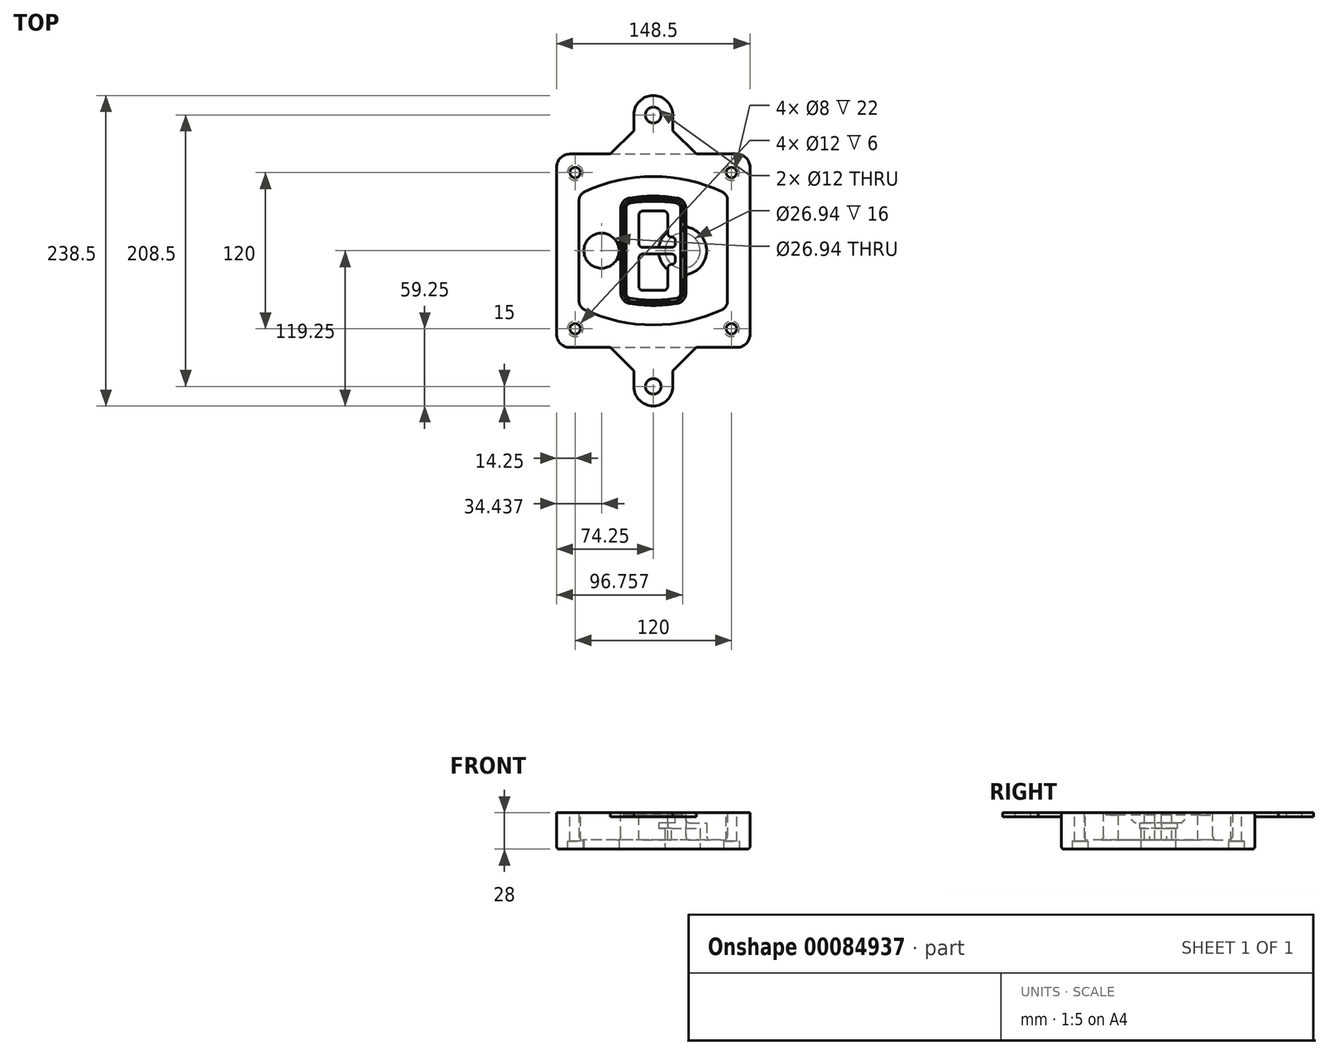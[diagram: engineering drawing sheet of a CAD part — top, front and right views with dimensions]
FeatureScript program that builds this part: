
annotation { "Feature Type Name" : "Feature", "Feature Type Description" : "" }
export const myFeature = defineFeature(function(context is Context, id is Id, definition is map)
    precondition{}
    {
        {
            var Q0;
            Q0=qCreatedBy(makeId("Top.planeOp"),FACE);
            var sketch = newSketch(context, id + "F0", { "sketchPlane" : qUnion([Q0])});
            skPoint(sketch, "E0.rect.middle", {"position": v(0, 0) * mm});
            skLineSegment(sketch, "E1.bottom", {"start": v(-64.25, -74.25) * mm, "end": v(64.25, -74.25) * mm});
            skLineSegment(sketch, "E1.top", {"start": v(-64.25, 74.25) * mm, "end": v(64.25, 74.25) * mm});
            skLineSegment(sketch, "E1.left", {"start": v(-74.25, -64.25) * mm, "end": v(-74.25, 64.25) * mm});
            skLineSegment(sketch, "E1.right", {"start": v(74.25, -64.25) * mm, "end": v(74.25, 64.25) * mm});
            skLineSegment(sketch, "E2", {"start": v(-74.25, 74.25) * mm, "end": v(74.25, -74.25) * mm, "construction": true});
            skLineSegment(sketch, "E3", {"start": v(74.25, 74.25) * mm, "end": v(-74.25, -74.25) * mm, "construction": true});
            skCircle(sketch, "E4", {"center": v(-60, 60) * mm, "radius": 4 * mm});
            skCircle(sketch, "E5", {"center": v(60, 60) * mm, "radius": 4 * mm});
            skCircle(sketch, "E6", {"center": v(60, -60) * mm, "radius": 4 * mm});
            skCircle(sketch, "E7", {"center": v(-60, -60) * mm, "radius": 4 * mm});
            skLineSegment(sketch, "E8", {"start": v(-60, 60) * mm, "end": v(60, 60) * mm, "construction": true});
            skLineSegment(sketch, "E9", {"start": v(60, 60) * mm, "end": v(60, -60) * mm, "construction": true});
            skLineSegment(sketch, "E10", {"start": v(60, -60) * mm, "end": v(-60, -60) * mm, "construction": true});
            skLineSegment(sketch, "E11", {"start": v(-60, -60) * mm, "end": v(-60, 60) * mm, "construction": true});
            skLineSegment(sketch, "E12", {"start": v(-60, 38.83) * mm, "end": v(-60, -38.83) * mm});
            skLineSegment(sketch, "E13", {"start": v(60, 38.83) * mm, "end": v(60, -38.83) * mm});
            skArc(sketch, "E14", {"start": v(54.26, 47.88) * mm, "mid": v(0, 60) * mm, "end": v(-54.26, 47.88) * mm});
            skArc(sketch, "E15", {"start": v(-54.26, -47.88) * mm, "mid": v(0, -60) * mm, "end": v(54.26, -47.88) * mm});
            skLineSegment(sketch, "E16", {"start": v(-60, 0) * mm, "end": v(60, 0) * mm, "construction": true});
            skPoint(sketch, "E17.visualSharp", {"position": v(-60, -45) * mm});
            skArc(sketch, "E17.filletArc", {"start": v(-60, -38.83) * mm, "mid": v(-58.44, -44.2) * mm, "end": v(-54.26, -47.88) * mm});
            skPoint(sketch, "E18.visualSharp", {"position": v(-60, 45) * mm});
            skArc(sketch, "E18.filletArc", {"start": v(-54.26, 47.88) * mm, "mid": v(-58.44, 44.2) * mm, "end": v(-60, 38.83) * mm});
            skPoint(sketch, "E19.visualSharp", {"position": v(60, 45) * mm});
            skArc(sketch, "E19.filletArc", {"start": v(60, 38.83) * mm, "mid": v(58.44, 44.2) * mm, "end": v(54.26, 47.88) * mm});
            skPoint(sketch, "E20.visualSharp", {"position": v(60, -45) * mm});
            skArc(sketch, "E20.filletArc", {"start": v(54.26, -47.88) * mm, "mid": v(58.44, -44.2) * mm, "end": v(60, -38.83) * mm});
            skPoint(sketch, "E21.visualSharp", {"position": v(-74.25, 74.25) * mm});
            skArc(sketch, "E21.filletArc", {"start": v(-64.25, 74.25) * mm, "mid": v(-71.32, 71.32) * mm, "end": v(-74.25, 64.25) * mm});
            skPoint(sketch, "E22.visualSharp", {"position": v(74.25, 74.25) * mm});
            skArc(sketch, "E22.filletArc", {"start": v(74.25, 64.25) * mm, "mid": v(71.32, 71.32) * mm, "end": v(64.25, 74.25) * mm});
            skPoint(sketch, "E23.visualSharp", {"position": v(74.25, -74.25) * mm});
            skArc(sketch, "E23.filletArc", {"start": v(64.25, -74.25) * mm, "mid": v(71.32, -71.32) * mm, "end": v(74.25, -64.25) * mm});
            skPoint(sketch, "E24.visualSharp", {"position": v(-74.25, -74.25) * mm});
            skArc(sketch, "E24.filletArc", {"start": v(-74.25, -64.25) * mm, "mid": v(-71.32, -71.32) * mm, "end": v(-64.25, -74.25) * mm});
            skArc(sketch, "E25.0", {"start": v(57, 38.83) * mm, "mid": v(55.9, 42.58) * mm, "end": v(52.98, 45.17) * mm});
            skLineSegment(sketch, "E25.1", {"start": v(57, 38.83) * mm, "end": v(57, -38.83) * mm});
            skArc(sketch, "E25.2", {"start": v(52.98, -45.17) * mm, "mid": v(55.9, -42.58) * mm, "end": v(57, -38.83) * mm});
            skArc(sketch, "E25.3", {"start": v(-52.98, -45.17) * mm, "mid": v(0, -57) * mm, "end": v(52.98, -45.17) * mm});
            skArc(sketch, "E25.4", {"start": v(-57, -38.83) * mm, "mid": v(-55.9, -42.58) * mm, "end": v(-52.98, -45.17) * mm});
            skArc(sketch, "E25.5", {"start": v(52.98, 45.17) * mm, "mid": v(0, 57) * mm, "end": v(-52.98, 45.17) * mm});
            skLineSegment(sketch, "E25.6", {"start": v(-57, 38.83) * mm, "end": v(-57, -38.83) * mm});
            skArc(sketch, "E25.7", {"start": v(-52.98, 45.17) * mm, "mid": v(-55.9, 42.58) * mm, "end": v(-57, 38.83) * mm});
            skArc(sketch, "E26.0", {"start": v(-55.96, 51.5) * mm, "mid": v(-61.82, 46.33) * mm, "end": v(-64, 38.83) * mm});
            skArc(sketch, "E26.1", {"start": v(55.96, 51.5) * mm, "mid": v(0, 64) * mm, "end": v(-55.96, 51.5) * mm});
            skArc(sketch, "E26.2", {"start": v(64, 38.83) * mm, "mid": v(61.82, 46.33) * mm, "end": v(55.96, 51.5) * mm});
            skLineSegment(sketch, "E26.3", {"start": v(64, 38.83) * mm, "end": v(64, -38.83) * mm});
            skArc(sketch, "E26.4", {"start": v(55.96, -51.5) * mm, "mid": v(61.82, -46.33) * mm, "end": v(64, -38.83) * mm});
            skLineSegment(sketch, "E26.5", {"start": v(-64, 38.83) * mm, "end": v(-64, -38.83) * mm});
            skArc(sketch, "E26.6", {"start": v(-55.96, -51.5) * mm, "mid": v(0, -64) * mm, "end": v(55.96, -51.5) * mm});
            skArc(sketch, "E26.7", {"start": v(-64, -38.83) * mm, "mid": v(-61.82, -46.33) * mm, "end": v(-55.96, -51.5) * mm});
            skSolve(sketch);
        }
        {
            var Q0;
            Q0=makeQuery(id+"F0.imprint","IMPRINT",FACE,{"disambiguationData":[TD([[makeQuery(id+"F0.imprint","IMPRINT",EDGE,{"derivedFrom":sQuery(id+"F0.wireOp",EDGE,"E1.bottom")}),1.0]])]});
            var Q1;
            Q1=makeQuery(id+"F0.imprint","IMPRINT",FACE,{"disambiguationData":[TD([[makeQuery(id+"F0.imprint","IMPRINT",EDGE,{"derivedFrom":sQuery(id+"F0.wireOp",EDGE,"E12")}),1.0]])]});
            var Q2;
            Q2=makeQuery(id+"F0.imprint","IMPRINT",FACE,{"disambiguationData":[TD([[makeQuery(id+"F0.imprint","IMPRINT",EDGE,{"derivedFrom":sQuery(id+"F0.wireOp",EDGE,"E25.0")}),1.0]])]});
            var Q3;
            Q3=makeQuery(id+"F0.imprint","IMPRINT",FACE,{"disambiguationData":[TD([[makeQuery(id+"F0.imprint","IMPRINT",EDGE,{"derivedFrom":sQuery(id+"F0.wireOp",EDGE,"E12")}),-1.0]])]});
            extrude(context, id + "F1", {"entities" : qUnion([Q0, Q1, Q2, Q3]), "oppositeDirection" : true, "depth" : 25 * mm});
        }
        {
            var Q0;
            Q0=makeQuery(id+"F0.imprint","IMPRINT",FACE,{"disambiguationData":[TD([[makeQuery(id+"F0.imprint","IMPRINT",EDGE,{"derivedFrom":sQuery(id+"F0.wireOp",EDGE,"E12")}),1.0]])]});
            extrude(context, id + "F2", {"entities" : qUnion([Q0]), "operationType" : NewBodyOperationType.ADD, "depth" : 3 * mm});
        }
        {
            var Q0;
            Q0=makeQuery(id+"F0.imprint","IMPRINT",FACE,{"disambiguationData":[TD([[makeQuery(id+"F0.imprint","IMPRINT",EDGE,{"derivedFrom":sQuery(id+"F0.wireOp",EDGE,"E25.0")}),1.0]])]});
            extrude(context, id + "F3", {"entities" : qUnion([Q0]), "operationType" : NewBodyOperationType.REMOVE, "oppositeDirection" : true, "depth" : 18 * mm});
        }
        {
            var Q0;
            Q0=makeQuery(id+"F2.opExtrude","CAP_FACE",FACE,{"disambiguationData":[OSD([sQuery(id+"F0.wireOp",EDGE,"E12"),sQuery(id+"F0.wireOp",EDGE,"E13"),sQuery(id+"F0.wireOp",EDGE,"E14"),sQuery(id+"F0.wireOp",EDGE,"E15"),sQuery(id+"F0.wireOp",EDGE,"E17.filletArc"),sQuery(id+"F0.wireOp",EDGE,"E18.filletArc"),sQuery(id+"F0.wireOp",EDGE,"E19.filletArc"),sQuery(id+"F0.wireOp",EDGE,"E20.filletArc"),sQuery(id+"F0.wireOp",EDGE,"E25.0"),sQuery(id+"F0.wireOp",EDGE,"E25.1"),sQuery(id+"F0.wireOp",EDGE,"E25.2"),sQuery(id+"F0.wireOp",EDGE,"E25.3"),sQuery(id+"F0.wireOp",EDGE,"E25.4"),sQuery(id+"F0.wireOp",EDGE,"E25.5"),sQuery(id+"F0.wireOp",EDGE,"E25.6"),sQuery(id+"F0.wireOp",EDGE,"E25.7")])],"isStart":false});
            var sketch = newSketch(context, id + "F4", { "sketchPlane" : qUnion([Q0])});
            skArc(sketch, "E27.0", {"start": v(-18.34, -40.45) * mm, "mid": v(0, -42) * mm, "end": v(18.34, -40.45) * mm});
            skArc(sketch, "E28.0", {"start": v(18.34, 40.45) * mm, "mid": v(0, 42) * mm, "end": v(-18.34, 40.45) * mm});
            skLineSegment(sketch, "E29", {"start": v(-25, 32.57) * mm, "end": v(-25, -32.57) * mm});
            skLineSegment(sketch, "E30", {"start": v(25, 32.57) * mm, "end": v(25, -32.57) * mm});
            skLineSegment(sketch, "E31", {"start": v(-25, 39.1) * mm, "end": v(25, 39.1) * mm, "construction": true});
            skLineSegment(sketch, "E32", {"start": v(-25, -39.1) * mm, "end": v(25, -39.1) * mm, "construction": true});
            skPoint(sketch, "E33.visualSharp", {"position": v(-25, 39.1) * mm});
            skArc(sketch, "E33.filletArc", {"start": v(-18.34, 40.45) * mm, "mid": v(-23.11, 37.73) * mm, "end": v(-25, 32.57) * mm});
            skPoint(sketch, "E34.visualSharp", {"position": v(25, 39.1) * mm});
            skArc(sketch, "E34.filletArc", {"start": v(25, 32.57) * mm, "mid": v(23.11, 37.73) * mm, "end": v(18.34, 40.45) * mm});
            skPoint(sketch, "E35.visualSharp", {"position": v(25, -39.1) * mm});
            skArc(sketch, "E35.filletArc", {"start": v(18.34, -40.45) * mm, "mid": v(23.11, -37.73) * mm, "end": v(25, -32.57) * mm});
            skPoint(sketch, "E36.visualSharp", {"position": v(-25, -39.1) * mm});
            skArc(sketch, "E36.filletArc", {"start": v(-25, -32.57) * mm, "mid": v(-23.11, -37.73) * mm, "end": v(-18.34, -40.45) * mm});
            skArc(sketch, "E37.0", {"start": v(52.98, 45.17) * mm, "mid": v(0, 57) * mm, "end": v(-52.98, 45.17) * mm});
            skArc(sketch, "E37.1", {"start": v(-52.98, 45.17) * mm, "mid": v(-55.9, 42.58) * mm, "end": v(-57, 38.83) * mm});
            skLineSegment(sketch, "E37.2", {"start": v(-57, 38.83) * mm, "end": v(-57, -38.83) * mm});
            skArc(sketch, "E37.3", {"start": v(-57, -38.83) * mm, "mid": v(-55.9, -42.58) * mm, "end": v(-52.98, -45.17) * mm});
            skArc(sketch, "E37.4", {"start": v(-52.98, -45.17) * mm, "mid": v(0, -57) * mm, "end": v(52.98, -45.17) * mm});
            skArc(sketch, "E37.5", {"start": v(52.98, -45.17) * mm, "mid": v(55.9, -42.58) * mm, "end": v(57, -38.83) * mm});
            skLineSegment(sketch, "E37.6", {"start": v(57, 38.83) * mm, "end": v(57, -38.83) * mm});
            skArc(sketch, "E37.7", {"start": v(57, 38.83) * mm, "mid": v(55.9, 42.58) * mm, "end": v(52.98, 45.17) * mm});
            skLineSegment(sketch, "E38.0", {"start": v(23, 32.57) * mm, "end": v(23, -32.57) * mm});
            skArc(sketch, "E38.1", {"start": v(18, -38.48) * mm, "mid": v(21.58, -36.44) * mm, "end": v(23, -32.57) * mm});
            skArc(sketch, "E38.2", {"start": v(-18, -38.48) * mm, "mid": v(0, -40) * mm, "end": v(18, -38.48) * mm});
            skArc(sketch, "E38.3", {"start": v(-23, -32.57) * mm, "mid": v(-21.58, -36.44) * mm, "end": v(-18, -38.48) * mm});
            skLineSegment(sketch, "E38.4", {"start": v(-23, 32.57) * mm, "end": v(-23, -32.57) * mm});
            skArc(sketch, "E38.5", {"start": v(23, 32.57) * mm, "mid": v(21.58, 36.44) * mm, "end": v(18, 38.48) * mm});
            skArc(sketch, "E38.6", {"start": v(-18, 38.48) * mm, "mid": v(-21.58, 36.44) * mm, "end": v(-23, 32.57) * mm});
            skArc(sketch, "E38.7", {"start": v(18, 38.48) * mm, "mid": v(0, 40) * mm, "end": v(-18, 38.48) * mm});
            skArc(sketch, "E39.0", {"start": v(21, 32.57) * mm, "mid": v(20.06, 35.15) * mm, "end": v(17.67, 36.5) * mm});
            skLineSegment(sketch, "E39.1", {"start": v(21, 32.57) * mm, "end": v(21, -32.57) * mm});
            skArc(sketch, "E39.2", {"start": v(17.67, -36.5) * mm, "mid": v(20.06, -35.15) * mm, "end": v(21, -32.57) * mm});
            skArc(sketch, "E39.3", {"start": v(-17.67, -36.5) * mm, "mid": v(0, -38) * mm, "end": v(17.67, -36.5) * mm});
            skArc(sketch, "E39.4", {"start": v(-21, -32.57) * mm, "mid": v(-20.06, -35.15) * mm, "end": v(-17.67, -36.5) * mm});
            skArc(sketch, "E39.5", {"start": v(17.67, 36.5) * mm, "mid": v(0, 38) * mm, "end": v(-17.67, 36.5) * mm});
            skLineSegment(sketch, "E39.6", {"start": v(-21, 32.57) * mm, "end": v(-21, -32.57) * mm});
            skArc(sketch, "E39.7", {"start": v(-17.67, 36.5) * mm, "mid": v(-20.06, 35.15) * mm, "end": v(-21, 32.57) * mm});
            skLineSegment(sketch, "E40", {"start": v(-25, 0) * mm, "end": v(25, 0) * mm, "construction": true});
            skLineSegment(sketch, "E41", {"start": v(-11, 5.5) * mm, "end": v(-11, 27.5) * mm});
            skLineSegment(sketch, "E42", {"start": v(-8, 30.5) * mm, "end": v(8, 30.5) * mm});
            skLineSegment(sketch, "E43", {"start": v(11, 27.5) * mm, "end": v(11, 13.5) * mm});
            skLineSegment(sketch, "E44", {"start": v(14, 10.5) * mm, "end": v(14, 10.5) * mm});
            skLineSegment(sketch, "E45", {"start": v(17, 7.5) * mm, "end": v(17, 5.5) * mm});
            skLineSegment(sketch, "E46", {"start": v(14, 2.5) * mm, "end": v(-8, 2.5) * mm});
            skPoint(sketch, "E47.visualSharp", {"position": v(-11, 30.5) * mm});
            skArc(sketch, "E47.filletArc", {"start": v(-8, 30.5) * mm, "mid": v(-10.12, 29.62) * mm, "end": v(-11, 27.5) * mm});
            skPoint(sketch, "E48.visualSharp", {"position": v(11, 30.5) * mm});
            skArc(sketch, "E48.filletArc", {"start": v(11, 27.5) * mm, "mid": v(10.12, 29.62) * mm, "end": v(8, 30.5) * mm});
            skPoint(sketch, "E49.visualSharp", {"position": v(11, 10.5) * mm});
            skArc(sketch, "E49.filletArc", {"start": v(11, 13.5) * mm, "mid": v(11.88, 11.38) * mm, "end": v(14, 10.5) * mm});
            skPoint(sketch, "E50.visualSharp", {"position": v(17, 10.5) * mm});
            skArc(sketch, "E50.filletArc", {"start": v(17, 7.5) * mm, "mid": v(16.12, 9.62) * mm, "end": v(14, 10.5) * mm});
            skPoint(sketch, "E51.visualSharp", {"position": v(17, 2.5) * mm});
            skArc(sketch, "E51.filletArc", {"start": v(14, 2.5) * mm, "mid": v(16.12, 3.38) * mm, "end": v(17, 5.5) * mm});
            skPoint(sketch, "E52.visualSharp", {"position": v(-11, 2.5) * mm});
            skArc(sketch, "E52.filletArc", {"start": v(-11, 5.5) * mm, "mid": v(-10.12, 3.38) * mm, "end": v(-8, 2.5) * mm});
            skLineSegment(sketch, "E53.0.MirrorCS", {"start": v(14, -2.5) * mm, "end": v(-8, -2.5) * mm});
            skArc(sketch, "E54.0.MirrorCS", {"start": v(-11, -5.5) * mm, "mid": v(-10.12, -3.38) * mm, "end": v(-8, -2.5) * mm});
            skLineSegment(sketch, "E55.0.MirrorCS", {"start": v(-11, -5.5) * mm, "end": v(-11, -27.5) * mm});
            skArc(sketch, "E56.0.MirrorCS", {"start": v(-8, -30.5) * mm, "mid": v(-10.12, -29.62) * mm, "end": v(-11, -27.5) * mm});
            skLineSegment(sketch, "E57.0.MirrorCS", {"start": v(-8, -30.5) * mm, "end": v(8, -30.5) * mm});
            skArc(sketch, "E58.0.MirrorCS", {"start": v(11, -27.5) * mm, "mid": v(10.12, -29.62) * mm, "end": v(8, -30.5) * mm});
            skLineSegment(sketch, "E59.0.MirrorCS", {"start": v(11, -27.5) * mm, "end": v(11, -13.5) * mm});
            skArc(sketch, "E60.0.MirrorCS", {"start": v(11, -13.5) * mm, "mid": v(11.88, -11.38) * mm, "end": v(14, -10.5) * mm});
            skArc(sketch, "E61.0.MirrorCS", {"start": v(17, -7.5) * mm, "mid": v(16.12, -9.62) * mm, "end": v(14, -10.5) * mm});
            skLineSegment(sketch, "E62.0.MirrorCS", {"start": v(17, -7.5) * mm, "end": v(17, -5.5) * mm});
            skArc(sketch, "E63.0.MirrorCS", {"start": v(14, -2.5) * mm, "mid": v(16.12, -3.38) * mm, "end": v(17, -5.5) * mm});
            skSolve(sketch);
        }
        {
            var Q0;
            Q0=makeQuery(id+"F4.imprint","IMPRINT",FACE,{"disambiguationData":[TD([[makeQuery(id+"F4.imprint","IMPRINT",EDGE,{"derivedFrom":sQuery(id+"F4.wireOp",EDGE,"E27.0")}),1.0]])]});
            var Q1;
            Q1=makeQuery(id+"F4.imprint","IMPRINT",FACE,{"disambiguationData":[TD([[makeQuery(id+"F4.imprint","IMPRINT",EDGE,{"derivedFrom":sQuery(id+"F4.wireOp",EDGE,"E38.0")}),-1.0]])]});
            var Q2;
            Q2=makeQuery(id+"F4.imprint","IMPRINT",FACE,{"disambiguationData":[TD([[makeQuery(id+"F4.imprint","IMPRINT",EDGE,{"derivedFrom":sQuery(id+"F4.wireOp",EDGE,"E39.0")}),1.0]])]});
            extrude(context, id + "F5", {"entities" : qUnion([Q0, Q1, Q2]), "operationType" : NewBodyOperationType.ADD, "endBound" : BoundingType.UP_TO_NEXT, "oppositeDirection" : true, "depth" : 25 * mm});
        }
        {
            var Q0;
            Q0=makeQuery(id+"F4.imprint","IMPRINT",FACE,{"disambiguationData":[TD([[makeQuery(id+"F4.imprint","IMPRINT",EDGE,{"derivedFrom":sQuery(id+"F4.wireOp",EDGE,"E38.0")}),-1.0]])]});
            extrude(context, id + "F6", {"entities" : qUnion([Q0]), "operationType" : NewBodyOperationType.REMOVE, "oppositeDirection" : true, "depth" : 2 * mm});
        }
        {
            var Q0;
            Q0=makeQuery(id+"F1.opExtrude","CAP_FACE",FACE,{"disambiguationData":[OSD([sQuery(id+"F0.wireOp",EDGE,"E1.bottom"),sQuery(id+"F0.wireOp",EDGE,"E1.top"),sQuery(id+"F0.wireOp",EDGE,"E1.left"),sQuery(id+"F0.wireOp",EDGE,"E1.right"),sQuery(id+"F0.wireOp",EDGE,"E4"),sQuery(id+"F0.wireOp",EDGE,"E5"),sQuery(id+"F0.wireOp",EDGE,"E6"),sQuery(id+"F0.wireOp",EDGE,"E7"),sQuery(id+"F0.wireOp",EDGE,"E21.filletArc"),sQuery(id+"F0.wireOp",EDGE,"E22.filletArc"),sQuery(id+"F0.wireOp",EDGE,"E23.filletArc"),sQuery(id+"F0.wireOp",EDGE,"E24.filletArc")])],"isStart":false});
            var sketch = newSketch(context, id + "F7", { "sketchPlane" : qUnion([Q0])});
            skCircle(sketch, "E64", {"center": v(22.5, 0) * mm, "radius": 13.47 * mm});
            skCircle(sketch, "E65", {"center": v(-39.81, 0) * mm, "radius": 13.47 * mm});
            skLineSegment(sketch, "E66", {"start": v(74.25, 0) * mm, "end": v(-74.25, 0) * mm});
            skCircle(sketch, "E67", {"center": v(22.5, 0) * mm, "radius": 18.47 * mm});
            skCircle(sketch, "E68", {"center": v(60, -60) * mm, "radius": 6 * mm});
            skCircle(sketch, "E69", {"center": v(-60, -60) * mm, "radius": 6 * mm});
            skCircle(sketch, "E70", {"center": v(-60, 60) * mm, "radius": 6 * mm});
            skCircle(sketch, "E71", {"center": v(60, 60) * mm, "radius": 6 * mm});
            skSolve(sketch);
        }
        {
            var Q0;
            {var subQ1=sQuery(id+"F7.wireOp",EDGE,"E66");var subQ4=sQuery(id+"F7.wireOp",EDGE,"E64");var subQ6=makeQuery(id+"F7.imprint","INTERSECT",VERTEX,{"disambiguationData":[OD(0.0)],"derivedFrom":[subQ4,subQ1]});Q0=makeQuery(id+"F7.imprint","IMPRINT",FACE,{"disambiguationData":[TD([[makeQuery(id+"F7.imprint","IMPRINT",EDGE,{"disambiguationData":[TD([[subQ6,-1.0]])],"derivedFrom":subQ4}),-1.0]])]});}
            var Q1;
            {var subQ0=sQuery(id+"F7.wireOp",EDGE,"E66");var subQ1=sQuery(id+"F7.wireOp",EDGE,"E64");var subQ3=makeQuery(id+"F7.imprint","INTERSECT",VERTEX,{"disambiguationData":[OD(0.0)],"derivedFrom":[subQ1,subQ0]});Q1=makeQuery(id+"F7.imprint","IMPRINT",FACE,{"disambiguationData":[TD([[makeQuery(id+"F7.imprint","IMPRINT",EDGE,{"disambiguationData":[TD([[subQ3,-1.0]])],"derivedFrom":subQ1}),1.0]])]});}
            var Q2;
            {var subQ0=sQuery(id+"F7.wireOp",EDGE,"E66");var subQ1=sQuery(id+"F7.wireOp",EDGE,"E64");var subQ3=makeQuery(id+"F7.imprint","INTERSECT",VERTEX,{"disambiguationData":[OD(0.0)],"derivedFrom":[subQ1,subQ0]});Q2=makeQuery(id+"F7.imprint","IMPRINT",FACE,{"disambiguationData":[TD([[makeQuery(id+"F7.imprint","IMPRINT",EDGE,{"disambiguationData":[TD([[subQ3,1.0]])],"derivedFrom":subQ1}),1.0]])]});}
            var Q3;
            {var subQ1=sQuery(id+"F7.wireOp",EDGE,"E66");var subQ4=sQuery(id+"F7.wireOp",EDGE,"E64");var subQ6=makeQuery(id+"F7.imprint","INTERSECT",VERTEX,{"disambiguationData":[OD(0.0)],"derivedFrom":[subQ4,subQ1]});Q3=makeQuery(id+"F7.imprint","IMPRINT",FACE,{"disambiguationData":[TD([[makeQuery(id+"F7.imprint","IMPRINT",EDGE,{"disambiguationData":[TD([[subQ6,1.0]])],"derivedFrom":subQ4}),-1.0]])]});}
            extrude(context, id + "F8", {"entities" : qUnion([Q0, Q1, Q2, Q3]), "operationType" : NewBodyOperationType.ADD, "oppositeDirection" : true, "depth" : 20 * mm});
        }
        {
            var Q0;
            {var subQ0=sQuery(id+"F7.wireOp",EDGE,"E66");var subQ1=sQuery(id+"F7.wireOp",EDGE,"E64");var subQ3=makeQuery(id+"F7.imprint","INTERSECT",VERTEX,{"disambiguationData":[OD(0.0)],"derivedFrom":[subQ1,subQ0]});Q0=makeQuery(id+"F7.imprint","IMPRINT",FACE,{"disambiguationData":[TD([[makeQuery(id+"F7.imprint","IMPRINT",EDGE,{"disambiguationData":[TD([[subQ3,-1.0]])],"derivedFrom":subQ1}),1.0]])]});}
            var Q1;
            {var subQ0=sQuery(id+"F7.wireOp",EDGE,"E66");var subQ1=sQuery(id+"F7.wireOp",EDGE,"E64");var subQ3=makeQuery(id+"F7.imprint","INTERSECT",VERTEX,{"disambiguationData":[OD(0.0)],"derivedFrom":[subQ1,subQ0]});Q1=makeQuery(id+"F7.imprint","IMPRINT",FACE,{"disambiguationData":[TD([[makeQuery(id+"F7.imprint","IMPRINT",EDGE,{"disambiguationData":[TD([[subQ3,1.0]])],"derivedFrom":subQ1}),1.0]])]});}
            extrude(context, id + "F9", {"entities" : qUnion([Q0, Q1]), "operationType" : NewBodyOperationType.REMOVE, "oppositeDirection" : true, "depth" : 16 * mm});
        }
        {
            var Q0;
            {var subQ0=sQuery(id+"F7.wireOp",EDGE,"E66");var subQ1=sQuery(id+"F7.wireOp",EDGE,"E65");var subQ3=makeQuery(id+"F7.imprint","INTERSECT",VERTEX,{"disambiguationData":[OD(0.0)],"derivedFrom":[subQ1,subQ0]});Q0=makeQuery(id+"F7.imprint","IMPRINT",FACE,{"disambiguationData":[TD([[makeQuery(id+"F7.imprint","IMPRINT",EDGE,{"disambiguationData":[TD([[subQ3,-1.0]])],"derivedFrom":subQ1}),1.0]])]});}
            var Q1;
            {var subQ0=sQuery(id+"F7.wireOp",EDGE,"E66");var subQ1=sQuery(id+"F7.wireOp",EDGE,"E65");var subQ3=makeQuery(id+"F7.imprint","INTERSECT",VERTEX,{"disambiguationData":[OD(0.0)],"derivedFrom":[subQ1,subQ0]});Q1=makeQuery(id+"F7.imprint","IMPRINT",FACE,{"disambiguationData":[TD([[makeQuery(id+"F7.imprint","IMPRINT",EDGE,{"disambiguationData":[TD([[subQ3,1.0]])],"derivedFrom":subQ1}),1.0]])]});}
            extrude(context, id + "F10", {"entities" : qUnion([Q0, Q1]), "operationType" : NewBodyOperationType.REMOVE, "oppositeDirection" : true, "depth" : 25 * mm});
        }
        {
            var Q0;
            Q0=makeQuery(id+"F7.imprint","IMPRINT",FACE,{"disambiguationData":[TD([[makeQuery(id+"F7.imprint","IMPRINT",EDGE,{"derivedFrom":sQuery(id+"F7.wireOp",EDGE,"E68")}),1.0]])]});
            var Q1;
            Q1=makeQuery(id+"F7.imprint","IMPRINT",FACE,{"disambiguationData":[TD([[makeQuery(id+"F7.imprint","IMPRINT",EDGE,{"derivedFrom":makeQuery(id+"F1.opExtrude","CAP_EDGE",EDGE,{"disambiguationData":[OSD([sQuery(id+"F0.wireOp",EDGE,"E5")])],"isStart":false})}),-1.0]])]});
            var Q2;
            Q2=makeQuery(id+"F7.imprint","IMPRINT",FACE,{"disambiguationData":[TD([[makeQuery(id+"F7.imprint","IMPRINT",EDGE,{"derivedFrom":sQuery(id+"F7.wireOp",EDGE,"E69")}),1.0]])]});
            var Q3;
            Q3=makeQuery(id+"F7.imprint","IMPRINT",FACE,{"disambiguationData":[TD([[makeQuery(id+"F7.imprint","IMPRINT",EDGE,{"derivedFrom":makeQuery(id+"F1.opExtrude","CAP_EDGE",EDGE,{"disambiguationData":[OSD([sQuery(id+"F0.wireOp",EDGE,"E4")])],"isStart":false})}),-1.0]])]});
            var Q4;
            Q4=makeQuery(id+"F7.imprint","IMPRINT",FACE,{"disambiguationData":[TD([[makeQuery(id+"F7.imprint","IMPRINT",EDGE,{"derivedFrom":sQuery(id+"F7.wireOp",EDGE,"E70")}),1.0]])]});
            var Q5;
            Q5=makeQuery(id+"F7.imprint","IMPRINT",FACE,{"disambiguationData":[TD([[makeQuery(id+"F7.imprint","IMPRINT",EDGE,{"derivedFrom":makeQuery(id+"F1.opExtrude","CAP_EDGE",EDGE,{"disambiguationData":[OSD([sQuery(id+"F0.wireOp",EDGE,"E7")])],"isStart":false})}),-1.0]])]});
            var Q6;
            Q6=makeQuery(id+"F7.imprint","IMPRINT",FACE,{"disambiguationData":[TD([[makeQuery(id+"F7.imprint","IMPRINT",EDGE,{"derivedFrom":sQuery(id+"F7.wireOp",EDGE,"E71")}),1.0]])]});
            var Q7;
            Q7=makeQuery(id+"F7.imprint","IMPRINT",FACE,{"disambiguationData":[TD([[makeQuery(id+"F7.imprint","IMPRINT",EDGE,{"derivedFrom":makeQuery(id+"F1.opExtrude","CAP_EDGE",EDGE,{"disambiguationData":[OSD([sQuery(id+"F0.wireOp",EDGE,"E6")])],"isStart":false})}),-1.0]])]});
            extrude(context, id + "F11", {"entities" : qUnion([Q0, Q1, Q2, Q3, Q4, Q5, Q6, Q7]), "operationType" : NewBodyOperationType.REMOVE, "oppositeDirection" : true, "depth" : 6 * mm});
        }
        {
            var Q0;
            Q0=makeQuery(id+"F9.boolean.opBoolean","COPY",FACE,{"derivedFrom":makeQuery(id+"F9.opExtrude","CAP_FACE",FACE,{"disambiguationData":[OSD([sQuery(id+"F7.wireOp",EDGE,"E64")])],"isStart":false})});
            var sketch = newSketch(context, id + "F12", { "sketchPlane" : qUnion([Q0])});
            skArc(sketch, "E72.0", {"start": v(11, 14.45) * mm, "mid": v(6.45, 9.13) * mm, "end": v(4.2, 2.5) * mm});
            skArc(sketch, "E72.1", {"start": v(4.2, -2.5) * mm, "mid": v(6.45, -9.13) * mm, "end": v(11, -14.45) * mm});
            skLineSegment(sketch, "E73", {"start": v(4.2, -2.5) * mm, "end": v(14, -2.5) * mm});
            skLineSegment(sketch, "E74.0", {"start": v(14, 2.5) * mm, "end": v(4.2, 2.5) * mm});
            skArc(sketch, "E74.1", {"start": v(14, 2.5) * mm, "mid": v(16.12, 3.38) * mm, "end": v(17, 5.5) * mm});
            skLineSegment(sketch, "E74.2", {"start": v(17, 7.5) * mm, "end": v(17, 5.5) * mm});
            skArc(sketch, "E74.3", {"start": v(17, 7.5) * mm, "mid": v(16.12, 9.62) * mm, "end": v(14, 10.5) * mm});
            skArc(sketch, "E74.4", {"start": v(11, 13.5) * mm, "mid": v(11.88, 11.38) * mm, "end": v(14, 10.5) * mm});
            skLineSegment(sketch, "E74.5", {"start": v(11, 14.45) * mm, "end": v(11, 13.5) * mm});
            skLineSegment(sketch, "E74.7", {"start": v(14, -2.5) * mm, "end": v(4.2, -2.5) * mm});
            skArc(sketch, "E74.8", {"start": v(14, -2.5) * mm, "mid": v(16.12, -3.38) * mm, "end": v(17, -5.5) * mm});
            skLineSegment(sketch, "E74.9", {"start": v(17, -7.5) * mm, "end": v(17, -5.5) * mm});
            skArc(sketch, "E74.10", {"start": v(17, -7.5) * mm, "mid": v(16.12, -9.62) * mm, "end": v(14, -10.5) * mm});
            skArc(sketch, "E74.11", {"start": v(11, -13.5) * mm, "mid": v(11.88, -11.38) * mm, "end": v(14, -10.5) * mm});
            skLineSegment(sketch, "E74.12", {"start": v(11, -14.45) * mm, "end": v(11, -13.5) * mm});
            skPoint(sketch, "E75.orphan", {"position": v(11, -27.5) * mm});
            skPoint(sketch, "E76.orphan", {"position": v(-8, -2.5) * mm});
            skPoint(sketch, "E77.orphan", {"position": v(-8, 2.5) * mm});
            skPoint(sketch, "E78.orphan", {"position": v(11, 27.5) * mm});
            skSolve(sketch);
        }
        {
            var Q0;
            {var subQ7=sQuery(id+"F12.wireOp",EDGE,"E72.0");var subQ14=sQuery(id+"F12.wireOp",EDGE,"E72.1");var subQ16=sQuery(id+"F12.wireOp",EDGE,"E74.1");var subQ18=sQuery(id+"F12.wireOp",EDGE,"E74.8");Q0=qUnion([makeQuery(id+"F12.imprint","IMPRINT",FACE,{"disambiguationData":[TD([[makeQuery(id+"F12.imprint","IMPRINT",EDGE,{"derivedFrom":subQ7}),1.0]])]}),makeQuery(id+"F12.imprint","IMPRINT",FACE,{"disambiguationData":[TD([[makeQuery(id+"F12.imprint","IMPRINT",EDGE,{"derivedFrom":subQ14}),1.0]])]}),makeQuery(id+"F12.imprint","IMPRINT",FACE,{"disambiguationData":[TD([[makeQuery(id+"F12.imprint","IMPRINT",EDGE,{"derivedFrom":subQ16}),1.0]])]}),makeQuery(id+"F12.imprint","IMPRINT",FACE,{"disambiguationData":[TD([[makeQuery(id+"F12.imprint","IMPRINT",EDGE,{"derivedFrom":subQ18}),-1.0]])]})]);}
            var Q1;
            Q1=makeQuery(id+"F5.boolean.opBoolean","SPLIT",FACE,{"disambiguationData":[TD([makeQuery(id+"F5.opExtrude","SWEPT_FACE",FACE,{"disambiguationData":[OSD([sQuery(id+"F4.wireOp",EDGE,"E41")])]})])],"derivedFrom":makeQuery(id+"F3.boolean.opBoolean","COPY",FACE,{"derivedFrom":makeQuery(id+"F3.opExtrude","CAP_FACE",FACE,{"disambiguationData":[OSD([sQuery(id+"F0.wireOp",EDGE,"E25.0"),sQuery(id+"F0.wireOp",EDGE,"E25.1"),sQuery(id+"F0.wireOp",EDGE,"E25.2"),sQuery(id+"F0.wireOp",EDGE,"E25.3"),sQuery(id+"F0.wireOp",EDGE,"E25.4"),sQuery(id+"F0.wireOp",EDGE,"E25.5"),sQuery(id+"F0.wireOp",EDGE,"E25.6"),sQuery(id+"F0.wireOp",EDGE,"E25.7")])],"isStart":false})})});
            extrude(context, id + "F13", {"entities" : qUnion([Q0]), "operationType" : NewBodyOperationType.REMOVE, "endBound" : BoundingType.UP_TO_SURFACE, "endBoundEntityFace" : qUnion([Q1]), "depth" : 25 * mm});
        }
        {
            var Q0;
            Q0=makeQuery(id+"F3.boolean.opBoolean","COPY",EDGE,{"derivedFrom":makeQuery(id+"F3.opExtrude","CAP_EDGE",EDGE,{"disambiguationData":[OSD([sQuery(id+"F0.wireOp",EDGE,"E25.6")])],"isStart":false})});
            var Q1;
            Q1=makeQuery(id+"F8.boolean.opBoolean","INTERSECT",EDGE,{"derivedFrom":[makeQuery(id+"F5.opExtrude","SWEPT_FACE",FACE,{"disambiguationData":[OSD([sQuery(id+"F4.wireOp",EDGE,"E30")])]}),makeQuery(id+"F8.opExtrude","CAP_FACE",FACE,{"disambiguationData":[OSD([sQuery(id+"F7.wireOp",EDGE,"E67")])],"isStart":false})]});
            var Q2;
            Q2=makeQuery(id+"F8.boolean.opBoolean","INTERSECT",EDGE,{"disambiguationData":[OD(1.0)],"derivedFrom":[makeQuery(id+"F5.opExtrude","SWEPT_FACE",FACE,{"disambiguationData":[OSD([sQuery(id+"F4.wireOp",EDGE,"E30")])]}),makeQuery(id+"F8.opExtrude","SWEPT_FACE",FACE,{"disambiguationData":[OSD([sQuery(id+"F7.wireOp",EDGE,"E67")])]})]});
            var Q3;
            {var subQ0=sQuery(id+"F4.wireOp",EDGE,"E30");Q3=makeQuery(id+"F8.boolean.opBoolean","SPLIT",EDGE,{"disambiguationData":[TD([makeQuery(id+"F5.opExtrude","SWEPT_FACE",FACE,{"disambiguationData":[OSD([sQuery(id+"F4.wireOp",EDGE,"E35.filletArc")])]})])],"derivedFrom":makeQuery(id+"F5.opExtrude","CAP_EDGE",EDGE,{"disambiguationData":[OSD([subQ0])],"isStart":false})});}
            var Q4;
            {var subQ0=sQuery(id+"F0.wireOp",EDGE,"E25.7");var subQ1=sQuery(id+"F0.wireOp",EDGE,"E25.1");var subQ2=sQuery(id+"F0.wireOp",EDGE,"E25.6");var subQ3=sQuery(id+"F0.wireOp",EDGE,"E25.5");var subQ4=sQuery(id+"F0.wireOp",EDGE,"E25.4");var subQ5=sQuery(id+"F0.wireOp",EDGE,"E25.0");var subQ6=sQuery(id+"F0.wireOp",EDGE,"E25.2");var subQ7=sQuery(id+"F0.wireOp",EDGE,"E25.3");Q4=makeQuery(id+"F8.boolean.opBoolean","INTERSECT",EDGE,{"derivedFrom":[makeQuery(id+"F5.boolean.opBoolean","SPLIT",FACE,{"disambiguationData":[TD([makeQuery(id+"F2.opExtrude","SWEPT_FACE",FACE,{"disambiguationData":[OSD([subQ5])]})])],"derivedFrom":makeQuery(id+"F3.boolean.opBoolean","COPY",FACE,{"derivedFrom":makeQuery(id+"F3.opExtrude","CAP_FACE",FACE,{"disambiguationData":[OSD([subQ5,subQ1,subQ6,subQ7,subQ4,subQ3,subQ2,subQ0])],"isStart":false})})}),makeQuery(id+"F8.opExtrude","SWEPT_FACE",FACE,{"disambiguationData":[OSD([sQuery(id+"F7.wireOp",EDGE,"E67")])]})]});}
            var Q5;
            Q5=makeQuery(id+"F8.boolean.opBoolean","INTERSECT",EDGE,{"disambiguationData":[OD(0.0)],"derivedFrom":[makeQuery(id+"F5.opExtrude","SWEPT_FACE",FACE,{"disambiguationData":[OSD([sQuery(id+"F4.wireOp",EDGE,"E30")])]}),makeQuery(id+"F8.opExtrude","SWEPT_FACE",FACE,{"disambiguationData":[OSD([sQuery(id+"F7.wireOp",EDGE,"E67")])]})]});
            fillet(context, id + "F14", {"entities" : qUnion([Q0, Q1, Q2, Q3, Q4, Q5]), "radius" : 3 * mm, "tangentPropagation" : true, "allowEdgeOverflow" : false});
        }
        {
            var Q0;
            Q0=makeQuery(id+"F1.opExtrude","CAP_EDGE",EDGE,{"disambiguationData":[OSD([sQuery(id+"F0.wireOp",EDGE,"E1.bottom")])],"isStart":false});
            fillet(context, id + "F15", {"entities" : qUnion([Q0]), "radius" : 2 * mm, "tangentPropagation" : true, "allowEdgeOverflow" : false});
        }
        {
            var Q0;
            {var subQ0=sQuery(id+"F0.wireOp",EDGE,"E22.filletArc");var subQ1=sQuery(id+"F0.wireOp",EDGE,"E7");var subQ2=sQuery(id+"F0.wireOp",EDGE,"E6");var subQ3=sQuery(id+"F0.wireOp",EDGE,"E5");var subQ4=sQuery(id+"F0.wireOp",EDGE,"E4");var subQ5=sQuery(id+"F0.wireOp",EDGE,"E1.bottom");var subQ6=sQuery(id+"F0.wireOp",EDGE,"E21.filletArc");var subQ7=sQuery(id+"F0.wireOp",EDGE,"E1.top");var subQ8=sQuery(id+"F0.wireOp",EDGE,"E1.left");var subQ9=sQuery(id+"F0.wireOp",EDGE,"E1.right");var subQ10=sQuery(id+"F0.wireOp",EDGE,"E23.filletArc");var subQ11=sQuery(id+"F0.wireOp",EDGE,"E24.filletArc");Q0=makeQuery(id+"F2.boolean.opBoolean","SPLIT",FACE,{"disambiguationData":[TD([makeQuery(id+"F1.opExtrude","SWEPT_FACE",FACE,{"disambiguationData":[OSD([subQ5])]})])],"derivedFrom":makeQuery(id+"F1.opExtrude","CAP_FACE",FACE,{"disambiguationData":[OSD([subQ5,subQ7,subQ8,subQ9,subQ4,subQ3,subQ2,subQ1,subQ6,subQ0,subQ10,subQ11])],"isStart":true})});}
            var sketch = newSketch(context, id + "F16", { "sketchPlane" : qUnion([Q0])});
            skCircle(sketch, "E79", {"center": v(0, 104.25) * mm, "radius": 6 * mm});
            skLineSegment(sketch, "E80", {"start": v(-15, 104.25) * mm, "end": v(-15, 92.25) * mm});
            skLineSegment(sketch, "E81", {"start": v(15, 104.25) * mm, "end": v(15, 92.25) * mm});
            skLineSegment(sketch, "E82", {"start": v(-15, 92.25) * mm, "end": v(-33, 74.25) * mm});
            skLineSegment(sketch, "E83", {"start": v(15, 92.25) * mm, "end": v(33, 74.25) * mm});
            skArc(sketch, "E84", {"start": v(15, 104.25) * mm, "mid": v(0, 119.25) * mm, "end": v(-15, 104.25) * mm});
            skLineSegment(sketch, "E85.MirrorCS", {"start": v(-15, -92.25) * mm, "end": v(-33, -74.25) * mm});
            skLineSegment(sketch, "E86.MirrorCS", {"start": v(-15, -104.25) * mm, "end": v(-15, -92.25) * mm});
            skArc(sketch, "E87.MirrorCS", {"start": v(15, -104.25) * mm, "mid": v(0, -119.25) * mm, "end": v(-15, -104.25) * mm});
            skLineSegment(sketch, "E88.MirrorCS", {"start": v(15, -104.25) * mm, "end": v(15, -92.25) * mm});
            skLineSegment(sketch, "E89.MirrorCS", {"start": v(15, -92.25) * mm, "end": v(33, -74.25) * mm});
            skCircle(sketch, "E90.MirrorC", {"center": v(0, -104.25) * mm, "radius": 6 * mm});
            skSolve(sketch);
        }
        {
            var Q0;
            Q0=makeQuery(id+"F16.imprint","IMPRINT",FACE,{"disambiguationData":[TD([[makeQuery(id+"F16.imprint","IMPRINT",EDGE,{"derivedFrom":sQuery(id+"F16.wireOp",EDGE,"E80")}),1.0]])]});
            var Q1;
            {var subQ0=sQuery(id+"F16.wireOp",EDGE,"E85.MirrorCS");Q1=makeQuery(id+"F16.imprint","IMPRINT",FACE,{"disambiguationData":[TD([[makeQuery(id+"F16.imprint","IMPRINT",EDGE,{"derivedFrom":subQ0}),-1.0]])]});}
            var Q2;
            Q2=makeQuery(id+"F16.imprint","IMPRINT",FACE,{"disambiguationData":[TD([[makeQuery(id+"F16.imprint","IMPRINT",EDGE,{"derivedFrom":makeQuery(id+"F1.opExtrude","CAP_EDGE",EDGE,{"disambiguationData":[OSD([sQuery(id+"F0.wireOp",EDGE,"E1.left")])],"isStart":true})}),-1.0]])]});
            var Q3;
            Q3=makeQuery(id+"F2.opExtrude","CAP_FACE",FACE,{"disambiguationData":[OSD([sQuery(id+"F0.wireOp",EDGE,"E12"),sQuery(id+"F0.wireOp",EDGE,"E13"),sQuery(id+"F0.wireOp",EDGE,"E14"),sQuery(id+"F0.wireOp",EDGE,"E15"),sQuery(id+"F0.wireOp",EDGE,"E17.filletArc"),sQuery(id+"F0.wireOp",EDGE,"E18.filletArc"),sQuery(id+"F0.wireOp",EDGE,"E19.filletArc"),sQuery(id+"F0.wireOp",EDGE,"E20.filletArc"),sQuery(id+"F0.wireOp",EDGE,"E25.0"),sQuery(id+"F0.wireOp",EDGE,"E25.1"),sQuery(id+"F0.wireOp",EDGE,"E25.2"),sQuery(id+"F0.wireOp",EDGE,"E25.3"),sQuery(id+"F0.wireOp",EDGE,"E25.4"),sQuery(id+"F0.wireOp",EDGE,"E25.5"),sQuery(id+"F0.wireOp",EDGE,"E25.6"),sQuery(id+"F0.wireOp",EDGE,"E25.7")])],"isStart":false});
            extrude(context, id + "F17", {"entities" : qUnion([Q0, Q1, Q2]), "operationType" : NewBodyOperationType.ADD, "endBound" : BoundingType.UP_TO_SURFACE, "endBoundEntityFace" : qUnion([Q3]), "depth" : 25 * mm});
        }
    });
